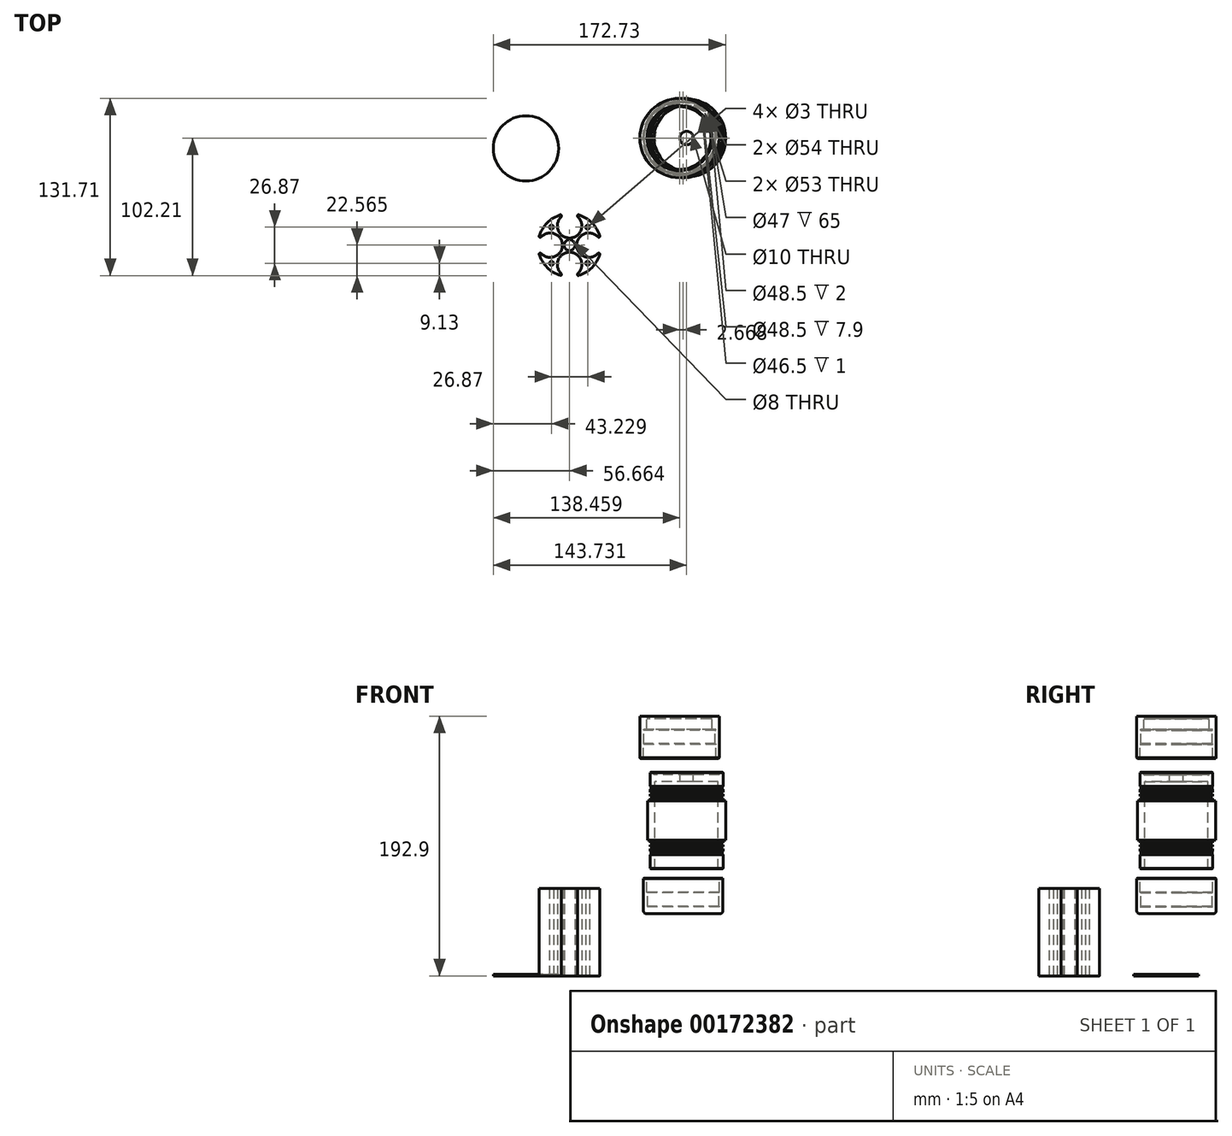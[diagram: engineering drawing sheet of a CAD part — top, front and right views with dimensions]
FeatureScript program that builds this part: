
annotation { "Feature Type Name" : "Feature", "Feature Type Description" : "" }
export const myFeature = defineFeature(function(context is Context, id is Id, definition is map)
    precondition{}
    {
        {
            var Q0;
            Q0=qCreatedBy(makeId("Top.planeOp"),FACE);
            var sketch = newSketch(context, id + "F0", { "sketchPlane" : qUnion([Q0])});
            skCircle(sketch, "E0", {"center": v(-74.52, -7.7) * mm, "radius": 24.25 * mm});
            skSolve(sketch);
        }
        {
            var Q0;
            Q0 = qSketchRegion(id + "F0", true);
            extrude(context, id + "F1", {"entities" : qUnion([Q0]), "depth" : 1 * mm});
        }
        {
            var Q0;
            Q0=qCreatedBy(makeId("Top.planeOp"),FACE);
            var sketch = newSketch(context, id + "F2", { "sketchPlane" : qUnion([Q0])});
            skArc(sketch, "E1", {"start": v(-48.75, -57.1) * mm, "mid": v(-58.72, -63.03) * mm, "end": v(-64.65, -73) * mm});
            skArc(sketch, "E2", {"start": v(-48.27, -58.55) * mm, "mid": v(-42.1, -74.35) * mm, "end": v(-35.94, -58.55) * mm});
            skArc(sketch, "E3.1.0", {"start": v(-63.2, -85.8) * mm, "mid": v(-47.4, -79.65) * mm, "end": v(-63.2, -73.48) * mm});
            skArc(sketch, "E3.2.0", {"start": v(-35.94, -100.74) * mm, "mid": v(-42.1, -84.95) * mm, "end": v(-48.27, -100.74) * mm});
            skArc(sketch, "E3.3.0", {"start": v(-21, -73.48) * mm, "mid": v(-36.8, -79.65) * mm, "end": v(-21, -85.8) * mm});
            skLineSegment(sketch, "E4", {"start": v(-48.1, -57.58) * mm, "end": v(-48.1, -58.18) * mm});
            skLineSegment(sketch, "E5", {"start": v(-36.1, -58.18) * mm, "end": v(-36.1, -57.58) * mm});
            skLineSegment(sketch, "E6.1.0", {"start": v(-63.57, -73.65) * mm, "end": v(-64.17, -73.65) * mm});
            skLineSegment(sketch, "E6.1.1", {"start": v(-64.17, -85.65) * mm, "end": v(-63.57, -85.65) * mm});
            skLineSegment(sketch, "E6.2.0", {"start": v(-48.1, -101.1) * mm, "end": v(-48.1, -101.7) * mm});
            skLineSegment(sketch, "E6.2.1", {"start": v(-36.1, -101.7) * mm, "end": v(-36.1, -101.1) * mm});
            skLineSegment(sketch, "E6.3.0", {"start": v(-20.64, -85.65) * mm, "end": v(-20.04, -85.65) * mm});
            skLineSegment(sketch, "E6.3.1", {"start": v(-20.04, -73.65) * mm, "end": v(-20.64, -73.65) * mm});
            skPoint(sketch, "E7.orphan", {"position": v(-48.1, -50.14) * mm});
            skPoint(sketch, "E8.orphan", {"position": v(-36.1, -51.64) * mm});
            skPoint(sketch, "E9.orphan", {"position": v(-48.1, -59.03) * mm});
            skPoint(sketch, "E10.orphan", {"position": v(-36.1, -60.53) * mm});
            skPoint(sketch, "E11.orphan", {"position": v(-12.6, -73.65) * mm});
            skPoint(sketch, "E12.orphan", {"position": v(-21.5, -73.65) * mm});
            skArc(sketch, "E13.trimOffspring", {"start": v(-19.56, -73) * mm, "mid": v(-25.49, -63.03) * mm, "end": v(-35.46, -57.1) * mm});
            skPoint(sketch, "E14.orphan", {"position": v(-14.1, -85.65) * mm});
            skPoint(sketch, "E15.orphan", {"position": v(-23, -85.65) * mm});
            skPoint(sketch, "E16.orphan", {"position": v(-36.1, -109.15) * mm});
            skArc(sketch, "E17.trimOffspring", {"start": v(-35.46, -102.19) * mm, "mid": v(-25.49, -96.26) * mm, "end": v(-19.56, -86.29) * mm});
            skPoint(sketch, "E18.orphan", {"position": v(-48.1, -107.65) * mm});
            skPoint(sketch, "E19.orphan", {"position": v(-48.1, -98.76) * mm});
            skPoint(sketch, "E20.orphan", {"position": v(-36.1, -100.26) * mm});
            skPoint(sketch, "E21.orphan", {"position": v(-62.72, -85.65) * mm});
            skPoint(sketch, "E22.orphan", {"position": v(-71.61, -85.65) * mm});
            skArc(sketch, "E23.trimOffspring", {"start": v(-64.65, -86.29) * mm, "mid": v(-58.72, -96.26) * mm, "end": v(-48.75, -102.19) * mm});
            skPoint(sketch, "E24.orphan", {"position": v(-70.11, -73.65) * mm});
            skPoint(sketch, "E25.orphan", {"position": v(-61.22, -73.65) * mm});
            skPoint(sketch, "E26.visualSharp", {"position": v(-48.1, -56.92) * mm});
            skArc(sketch, "E26.filletArc", {"start": v(-48.1, -57.58) * mm, "mid": v(-48.3, -57.18) * mm, "end": v(-48.75, -57.1) * mm});
            skPoint(sketch, "E27.visualSharp", {"position": v(-48.1, -58.4) * mm});
            skArc(sketch, "E27.filletArc", {"start": v(-48.27, -58.55) * mm, "mid": v(-48.15, -58.38) * mm, "end": v(-48.1, -58.18) * mm});
            skPoint(sketch, "E28.visualSharp", {"position": v(-36.1, -56.92) * mm});
            skArc(sketch, "E28.filletArc", {"start": v(-35.46, -57.1) * mm, "mid": v(-35.9, -57.18) * mm, "end": v(-36.1, -57.58) * mm});
            skPoint(sketch, "E29.visualSharp", {"position": v(-36.1, -58.4) * mm});
            skArc(sketch, "E29.filletArc", {"start": v(-36.1, -58.18) * mm, "mid": v(-36.06, -58.38) * mm, "end": v(-35.94, -58.55) * mm});
            skPoint(sketch, "E30.visualSharp", {"position": v(-19.38, -73.65) * mm});
            skArc(sketch, "E30.filletArc", {"start": v(-20.04, -73.65) * mm, "mid": v(-19.64, -73.44) * mm, "end": v(-19.56, -73) * mm});
            skPoint(sketch, "E31.visualSharp", {"position": v(-20.86, -73.65) * mm});
            skArc(sketch, "E31.filletArc", {"start": v(-21, -73.48) * mm, "mid": v(-20.84, -73.6) * mm, "end": v(-20.64, -73.65) * mm});
            skPoint(sketch, "E32.visualSharp", {"position": v(-19.38, -85.65) * mm});
            skArc(sketch, "E32.filletArc", {"start": v(-19.56, -86.29) * mm, "mid": v(-19.64, -85.85) * mm, "end": v(-20.04, -85.65) * mm});
            skPoint(sketch, "E33.visualSharp", {"position": v(-20.86, -85.65) * mm});
            skArc(sketch, "E33.filletArc", {"start": v(-20.64, -85.65) * mm, "mid": v(-20.84, -85.69) * mm, "end": v(-21, -85.8) * mm});
            skPoint(sketch, "E34.visualSharp", {"position": v(-36.1, -102.37) * mm});
            skArc(sketch, "E34.filletArc", {"start": v(-36.1, -101.7) * mm, "mid": v(-35.9, -102.1) * mm, "end": v(-35.46, -102.19) * mm});
            skPoint(sketch, "E35.visualSharp", {"position": v(-36.1, -100.89) * mm});
            skArc(sketch, "E35.filletArc", {"start": v(-35.94, -100.74) * mm, "mid": v(-36.06, -100.9) * mm, "end": v(-36.1, -101.1) * mm});
            skPoint(sketch, "E36.visualSharp", {"position": v(-48.1, -100.89) * mm});
            skArc(sketch, "E36.filletArc", {"start": v(-48.1, -101.1) * mm, "mid": v(-48.15, -100.9) * mm, "end": v(-48.27, -100.74) * mm});
            skPoint(sketch, "E37.visualSharp", {"position": v(-48.1, -102.37) * mm});
            skArc(sketch, "E37.filletArc", {"start": v(-48.75, -102.19) * mm, "mid": v(-48.3, -102.1) * mm, "end": v(-48.1, -101.7) * mm});
            skPoint(sketch, "E38.visualSharp", {"position": v(-64.83, -85.65) * mm});
            skArc(sketch, "E38.filletArc", {"start": v(-64.17, -85.65) * mm, "mid": v(-64.57, -85.85) * mm, "end": v(-64.65, -86.29) * mm});
            skPoint(sketch, "E39.visualSharp", {"position": v(-63.35, -85.65) * mm});
            skArc(sketch, "E39.filletArc", {"start": v(-63.2, -85.8) * mm, "mid": v(-63.37, -85.69) * mm, "end": v(-63.57, -85.65) * mm});
            skPoint(sketch, "E40.visualSharp", {"position": v(-64.83, -73.65) * mm});
            skArc(sketch, "E40.filletArc", {"start": v(-64.65, -73) * mm, "mid": v(-64.57, -73.44) * mm, "end": v(-64.17, -73.65) * mm});
            skPoint(sketch, "E41.visualSharp", {"position": v(-63.35, -73.65) * mm});
            skArc(sketch, "E41.filletArc", {"start": v(-63.57, -73.65) * mm, "mid": v(-63.37, -73.6) * mm, "end": v(-63.2, -73.48) * mm});
            skCircle(sketch, "E42", {"center": v(-42.1, -79.65) * mm, "radius": 4 * mm});
            skLineSegment(sketch, "E43", {"start": v(-63.53, -58.22) * mm, "end": v(-42.1, -79.65) * mm, "construction": true});
            skCircle(sketch, "E44", {"center": v(-55.54, -66.21) * mm, "radius": 1.5 * mm});
            skCircle(sketch, "E45.1.0", {"center": v(-55.54, -93.08) * mm, "radius": 1.5 * mm});
            skCircle(sketch, "E45.2.0", {"center": v(-28.67, -93.08) * mm, "radius": 1.5 * mm});
            skCircle(sketch, "E45.3.0", {"center": v(-28.67, -66.21) * mm, "radius": 1.5 * mm});
            skSolve(sketch);
        }
        {
            var Q0;
            Q0 = qSketchRegion(id + "F2", true);
            extrude(context, id + "F3", {"entities" : qUnion([Q0]), "depth" : 65 * mm});
        }
        {
            var Q0;
            Q0=qCreatedBy(makeId("Front.planeOp"),FACE);
            var sketch = newSketch(context, id + "F4", { "sketchPlane" : qUnion([Q0])});
            skLineSegment(sketch, "E46", {"start": v(21.46, 79.48) * mm, "end": v(21.46, 144.48) * mm});
            skLineSegment(sketch, "E47", {"start": v(18.46, 79.48) * mm, "end": v(17.96, 79.98) * mm});
            skLineSegment(sketch, "E48", {"start": v(17.96, 79.98) * mm, "end": v(17.96, 89.98) * mm});
            skLineSegment(sketch, "E49", {"start": v(17.96, 89.98) * mm, "end": v(18.46, 90.48) * mm});
            skLineSegment(sketch, "E50", {"start": v(17.96, 100.98) * mm, "end": v(15.96, 100.98) * mm});
            skLineSegment(sketch, "E51", {"start": v(15.96, 100.98) * mm, "end": v(15.96, 129.98) * mm});
            skLineSegment(sketch, "E52", {"start": v(44.96, 138.27) * mm, "end": v(44.96, 71.06) * mm, "construction": true});
            skLineSegment(sketch, "E53", {"start": v(17.96, 94.48) * mm, "end": v(18.96, 94.48) * mm});
            skLineSegment(sketch, "E54", {"start": v(18.96, 94.48) * mm, "end": v(18.96, 95.98) * mm});
            skLineSegment(sketch, "E55", {"start": v(18.96, 95.98) * mm, "end": v(17.96, 95.98) * mm});
            skLineSegment(sketch, "E56", {"start": v(17.96, 95.98) * mm, "end": v(17.96, 97.48) * mm});
            skLineSegment(sketch, "E57", {"start": v(17.96, 97.48) * mm, "end": v(18.96, 97.48) * mm});
            skLineSegment(sketch, "E58", {"start": v(18.96, 97.48) * mm, "end": v(18.96, 98.98) * mm});
            skLineSegment(sketch, "E59", {"start": v(18.96, 98.98) * mm, "end": v(17.96, 98.98) * mm});
            skLineSegment(sketch, "E60", {"start": v(17.96, 98.98) * mm, "end": v(17.96, 100.98) * mm});
            skLineSegment(sketch, "E61", {"start": v(21.46, 79.48) * mm, "end": v(18.46, 79.48) * mm});
            skLineSegment(sketch, "E62", {"start": v(18.46, 90.48) * mm, "end": v(18.46, 92.48) * mm});
            skLineSegment(sketch, "E63", {"start": v(18.46, 92.48) * mm, "end": v(17.96, 92.48) * mm});
            skLineSegment(sketch, "E64", {"start": v(17.96, 92.48) * mm, "end": v(17.96, 94.48) * mm});
            skLineSegment(sketch, "E65", {"start": v(21.46, 144.48) * mm, "end": v(39.96, 144.48) * mm});
            skLineSegment(sketch, "E66", {"start": v(39.96, 144.48) * mm, "end": v(39.96, 149.48) * mm});
            skLineSegment(sketch, "E67", {"start": v(39.96, 149.48) * mm, "end": v(20.71, 149.48) * mm});
            skLineSegment(sketch, "E68", {"start": v(18.46, 151.48) * mm, "end": v(20.71, 151.48) * mm});
            skLineSegment(sketch, "E69", {"start": v(20.71, 151.48) * mm, "end": v(20.71, 149.48) * mm});
            skLineSegment(sketch, "E70", {"start": v(17.96, 150.98) * mm, "end": v(17.96, 140.98) * mm});
            skLineSegment(sketch, "E71", {"start": v(17.96, 129.98) * mm, "end": v(15.96, 129.98) * mm});
            skLineSegment(sketch, "E72", {"start": v(18.46, 151.48) * mm, "end": v(17.96, 150.98) * mm});
            skLineSegment(sketch, "E73", {"start": v(17.96, 140.98) * mm, "end": v(18.46, 140.48) * mm});
            skLineSegment(sketch, "E74", {"start": v(18.46, 140.48) * mm, "end": v(18.46, 138.48) * mm});
            skLineSegment(sketch, "E75", {"start": v(18.46, 138.48) * mm, "end": v(17.96, 138.48) * mm});
            skLineSegment(sketch, "E76", {"start": v(17.96, 138.48) * mm, "end": v(17.96, 136.48) * mm});
            skLineSegment(sketch, "E77", {"start": v(17.96, 136.48) * mm, "end": v(18.96, 136.48) * mm});
            skLineSegment(sketch, "E78", {"start": v(18.96, 136.48) * mm, "end": v(18.96, 134.98) * mm});
            skLineSegment(sketch, "E79", {"start": v(18.96, 134.98) * mm, "end": v(17.96, 134.98) * mm});
            skLineSegment(sketch, "E80", {"start": v(17.96, 133.48) * mm, "end": v(18.96, 133.48) * mm});
            skLineSegment(sketch, "E81", {"start": v(18.96, 133.48) * mm, "end": v(18.96, 131.98) * mm});
            skLineSegment(sketch, "E82", {"start": v(18.96, 131.98) * mm, "end": v(17.96, 131.98) * mm});
            skLineSegment(sketch, "E83.trimOffspring", {"start": v(17.96, 134.98) * mm, "end": v(17.96, 133.48) * mm});
            skLineSegment(sketch, "E84.trimOffspring", {"start": v(17.96, 131.98) * mm, "end": v(17.96, 129.98) * mm});
            skSolve(sketch);
        }
        {
            var Q0;
            Q0=makeQuery(id+"F4.imprint","IMPRINT",FACE,{"disambiguationData":[TD([[makeQuery(id+"F4.imprint","IMPRINT",EDGE,{"derivedFrom":sQuery(id+"F4.wireOp",EDGE,"E46")}),1.0]])]});
            var Q1;
            Q1=sQuery(id+"F4.wireOp",EDGE,"E52");
            revolve(context, id + "F5", {"entities" : qUnion([Q0]), "axis" : qUnion([Q1]), "revolveType" : RevolveType.FULL});
        }
        {
            var Q0;
            Q0=qCreatedBy(makeId("Front.planeOp"),FACE);
            var sketch = newSketch(context, id + "F6", { "sketchPlane" : qUnion([Q0])});
            skLineSegment(sketch, "E85", {"start": v(42.36, 70.97) * mm, "end": v(42.36, 51.24) * mm, "construction": true});
            skLineSegment(sketch, "E86", {"start": v(42.36, 51.24) * mm, "end": v(15.86, 51.24) * mm});
            skLineSegment(sketch, "E87", {"start": v(15.86, 51.74) * mm, "end": v(15.86, 61.74) * mm});
            skLineSegment(sketch, "E88", {"start": v(15.36, 72.74) * mm, "end": v(12.86, 72.74) * mm});
            skLineSegment(sketch, "E89", {"start": v(12.86, 72.74) * mm, "end": v(12.86, 48.24) * mm});
            skLineSegment(sketch, "E90", {"start": v(14.86, 46.24) * mm, "end": v(42.36, 46.24) * mm});
            skLineSegment(sketch, "E91", {"start": v(42.36, 46.24) * mm, "end": v(42.36, 51.24) * mm});
            skLineSegment(sketch, "E92", {"start": v(15.86, 51.24) * mm, "end": v(15.36, 51.24) * mm});
            skLineSegment(sketch, "E93", {"start": v(15.86, 51.74) * mm, "end": v(15.36, 51.24) * mm});
            skLineSegment(sketch, "E94", {"start": v(16.15, 61.74) * mm, "end": v(19.68, 61.74) * mm, "construction": true});
            skLineSegment(sketch, "E95", {"start": v(15.86, 61.74) * mm, "end": v(15.36, 62.24) * mm});
            skLineSegment(sketch, "E96", {"start": v(15.36, 62.24) * mm, "end": v(15.36, 72.74) * mm});
            skPoint(sketch, "E97.visualSharp", {"position": v(12.86, 46.24) * mm});
            skArc(sketch, "E97.filletArc", {"start": v(12.86, 48.24) * mm, "mid": v(13.44, 46.83) * mm, "end": v(14.86, 46.24) * mm});
            skSolve(sketch);
        }
        {
            var Q0;
            Q0=makeQuery(id+"F6.imprint","IMPRINT",FACE,{"disambiguationData":[TD([[makeQuery(id+"F6.imprint","IMPRINT",EDGE,{"derivedFrom":sQuery(id+"F6.wireOp",EDGE,"E86")}),1.0]])]});
            var Q1;
            Q1=sQuery(id+"F6.wireOp",EDGE,"E85");
            revolve(context, id + "F7", {"entities" : qUnion([Q0]), "axis" : qUnion([Q1]), "revolveType" : RevolveType.FULL});
        }
        {
            var Q0;
            Q0=makeQuery(id+"F7.opRevolve","SWEPT_EDGE",EDGE,{"disambiguationData":[OSD([sQuery(id+"F6.wireOp",EDGE,"E88"),sQuery(id+"F6.wireOp",EDGE,"E96")])]});
            chamfer(context, id + "F8", {"entities" : qUnion([Q0]), "width" : 0.5 * mm, "tangentPropagation" : true});
        }
        {
            var Q0;
            Q0=makeQuery(id+"F7.opRevolve","SWEPT_EDGE",EDGE,{"disambiguationData":[OSD([sQuery(id+"F6.wireOp",EDGE,"E88"),sQuery(id+"F6.wireOp",EDGE,"E89")])]});
            chamfer(context, id + "F9", {"entities" : qUnion([Q0]), "width" : .5 * mm, "tangentPropagation" : true});
        }
        {
            var Q0;
            Q0=qCreatedBy(makeId("Front.planeOp"),FACE);
            var sketch = newSketch(context, id + "F10", { "sketchPlane" : qUnion([Q0])});
            skLineSegment(sketch, "E98", {"start": v(12.69, 161.5) * mm, "end": v(12.69, 183) * mm});
            skLineSegment(sketch, "E99", {"start": v(39.69, 193.18) * mm, "end": v(39.69, 161.5) * mm, "construction": true});
            skLineSegment(sketch, "E100", {"start": v(10.19, 191.4) * mm, "end": v(10.19, 161.5) * mm});
            skLineSegment(sketch, "E101", {"start": v(10.19, 161.5) * mm, "end": v(12.69, 161.5) * mm});
            skLineSegment(sketch, "E102", {"start": v(12.69, 183) * mm, "end": v(15.44, 183) * mm});
            skLineSegment(sketch, "E103", {"start": v(15.44, 183) * mm, "end": v(15.44, 190.9) * mm});
            skLineSegment(sketch, "E104", {"start": v(15.44, 190.9) * mm, "end": v(16.44, 190.9) * mm});
            skLineSegment(sketch, "E105", {"start": v(16.44, 190.9) * mm, "end": v(16.44, 191.9) * mm});
            skLineSegment(sketch, "E106", {"start": v(16.44, 191.9) * mm, "end": v(15.44, 192.9) * mm});
            skLineSegment(sketch, "E107", {"start": v(15.44, 192.9) * mm, "end": v(10.19, 192.9) * mm});
            skLineSegment(sketch, "E108", {"start": v(10.19, 192.9) * mm, "end": v(10.19, 191.4) * mm});
            skLineSegment(sketch, "E109", {"start": v(12.69, 183) * mm, "end": v(13.19, 182.5) * mm});
            skLineSegment(sketch, "E110", {"start": v(13.19, 182.5) * mm, "end": v(13.19, 172.5) * mm});
            skLineSegment(sketch, "E111", {"start": v(13.19, 172.5) * mm, "end": v(12.69, 172) * mm});
            skSolve(sketch);
        }
        {
            var Q0;
            Q0 = qSketchRegion(id + "F10", true);
            var Q1;
            Q1=sQuery(id+"F10.wireOp",EDGE,"E99");
            revolve(context, id + "F11", {"entities" : qUnion([Q0]), "axis" : qUnion([Q1]), "revolveType" : RevolveType.FULL});
        }
        {
            var Q0;
            Q0=makeQuery(id+"F11.opRevolve","SWEPT_EDGE",EDGE,{"disambiguationData":[OSD([sQuery(id+"F10.wireOp",EDGE,"E100"),sQuery(id+"F10.wireOp",EDGE,"E101")])]});
            var Q1;
            Q1=makeQuery(id+"F11.opRevolve","SWEPT_EDGE",EDGE,{"disambiguationData":[OSD([sQuery(id+"F10.wireOp",EDGE,"E98"),sQuery(id+"F10.wireOp",EDGE,"E101")])]});
            chamfer(context, id + "F12", {"entities" : qUnion([Q0, Q1]), "width" : .5 * mm, "tangentPropagation" : true});
        }
    });
